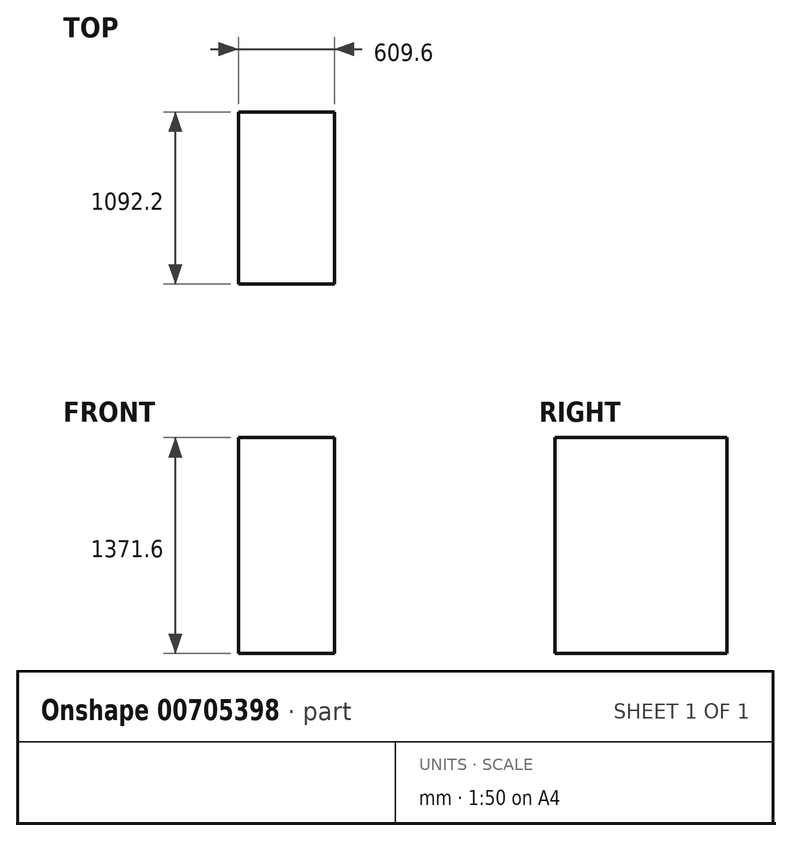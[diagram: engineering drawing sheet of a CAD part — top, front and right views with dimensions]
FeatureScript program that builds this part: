
annotation { "Feature Type Name" : "Feature", "Feature Type Description" : "" }
export const myFeature = defineFeature(function(context is Context, id is Id, definition is map)
    precondition{}
    {
        {
            var Q0;
            Q0=qCreatedBy(makeId("Top.planeOp"),FACE);
            var sketch = newSketch(context, id + "F0", { "sketchPlane" : qUnion([Q0])});
            skLineSegment(sketch, "E0.bottom", {"start": v(0, 0) * mm, "end": v(609.6, 0) * mm});
            skLineSegment(sketch, "E0.top", {"start": v(0, 1092.2) * mm, "end": v(609.6, 1092.2) * mm});
            skLineSegment(sketch, "E0.left", {"start": v(0, 0) * mm, "end": v(0, 1092.2) * mm});
            skLineSegment(sketch, "E0.right", {"start": v(609.6, 0) * mm, "end": v(609.6, 1092.2) * mm});
            skSolve(sketch);
        }
        {
            var Q0;
            Q0=makeQuery(id+"F0.imprint","IMPRINT",FACE,{"disambiguationData":[TD([[makeQuery(id+"F0.imprint","IMPRINT",EDGE,{"derivedFrom":sQuery(id+"F0.wireOp",EDGE,"E0.bottom")}),1.0]])]});
            extrude(context, id + "F1", {"entities" : qUnion([Q0]), "depth" : 1371.6 * mm, "offsetDistance" : 25.4 * mm});
        }
    });
